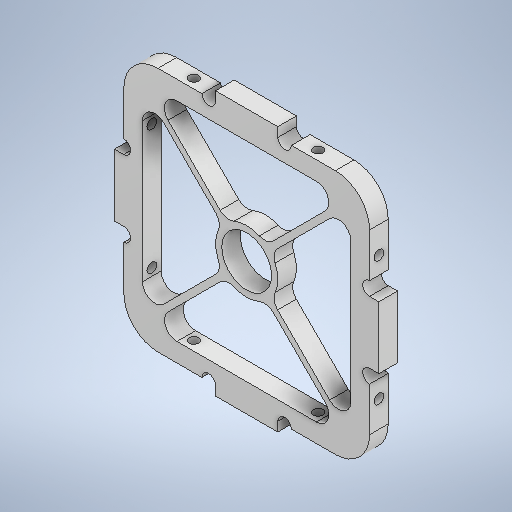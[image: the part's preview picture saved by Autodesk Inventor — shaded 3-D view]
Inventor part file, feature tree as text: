
AUTODESK INVENTOR PART (.ipt)
format: ipt  version: 2025.1 (Build 291241000, 241)  size: 476,160 bytes
history: native  units: mm
features: sketch x5, extrude x3, other x2, fillet x2, hole x2, projected_geometry x1
ambient origin geometry x8: Origin, YZ Plane, XZ Plane, XY Plane, X Axis, Y Axis, Z Axis, Center Point
bodies: Body1 (feature_tree)
feature tree (15):
  other  "ソリッド1"
  extrude  "押し出し1"  Depth=39.5mm
  extrude  "押し出し2"  Depth=1.5mm
  fillet  "フィレット1"  Radius=10.0mm
  hole  "穴1"  [1 undecoded]
  hole  "穴2"  [1 undecoded]
  extrude  "押し出し3"  Depth=3.0mm TaperAngle=0.0deg
  fillet  "フィレット2"  Radius=5.0mm
  sketch  "スケッチ1"
  other  "スケッチ円形状パターン1"
  sketch  "スケッチ2"
  sketch  "スケッチ3"
  sketch  "スケッチ4"
  sketch  "スケッチ5"
  projected_geometry  "投影ループ1"
note: 2 required parameter values undecoded (feature->parameter linkage not recoverable at this tier; creation-order binding heuristic only, values carry confidence <= 0.55)
